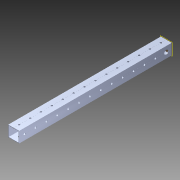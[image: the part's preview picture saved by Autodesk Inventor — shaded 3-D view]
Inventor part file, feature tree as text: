
AUTODESK INVENTOR PART (.ipt)
format: ipt  version: 2014 SP1 (Build 180222100, 222)  size: 1,288,704 bytes
history: native  units: in
note: dims shown in document units (in); Inventor stores cm internally (conversion verified against a paired STEP export)
features: extrude x4, sketch x4, pattern_circular x1, other x1, plane x1, imported_body x1
ambient origin geometry x8: Origin, YZ Plane, XZ Plane, XY Plane, X Axis, Y Axis, Z Axis, Center Point
bodies: Body1 (feature_tree)
feature tree (12):
  pattern_circular  "CirPattern2"
  other  "217-3426-STEP1"
  plane  "Work Plane1"
  extrude  "Extrusion1"  Depth=3937.0079in TaperAngle=0.0deg
  extrude  "Extrusion2"  Depth=1.0in TaperAngle=0.0deg
  extrude  "Extrusion3"  Depth=39.3701in TaperAngle=0.0deg
  extrude  "Extrusion4"  [1 undecoded]
  imported_body  "Base1"
  sketch  "Sketch1"  dims[d0=-21.0in d1=3937.0079in d2=0.0in]
  sketch  "Sketch3"  dims[d3=1.0in d4=0.0in d5=6.0in d6=0.0in]
  sketch  "Sketch4"  dims[d7=0.375in d8=39.3701in d9=0.0in]
  sketch  "Sketch5"
note: 1 required parameter value undecoded (feature->parameter linkage not recoverable at this tier; creation-order binding heuristic only, values carry confidence <= 0.55)
